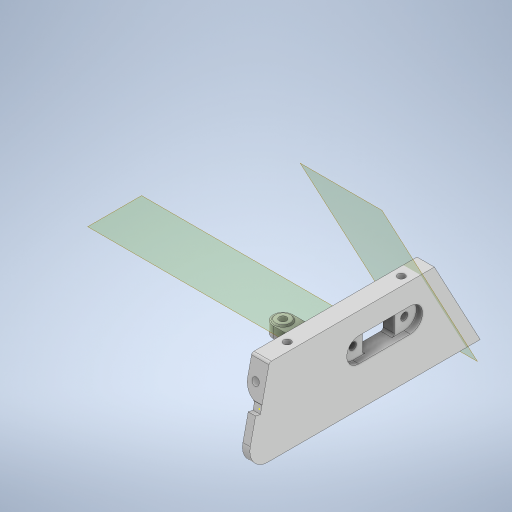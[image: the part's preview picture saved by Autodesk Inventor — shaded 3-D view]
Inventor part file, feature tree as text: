
AUTODESK INVENTOR PART (.ipt)
format: ipt  version: 2023 (Build 270158000, 158)  size: 805,888 bytes
history: native  units: mm
features: extrude x29, sketch x29, reference x17, other x16, projected_geometry x15, fillet x9, chamfer x1
ambient origin geometry x8: Origin, YZ Plane, XZ Plane, XY Plane, X Axis, Y Axis, Z Axis, Center Point
bodies: Body1 (feature_tree)
feature tree (116):
  other  "Bryła1"
  extrude  "Wyciągnięcie proste1"  Depth=6.5mm TaperAngle=0.0deg
  extrude  "Wyciągnięcie proste2"  Depth=3.7mm TaperAngle=0.0deg
  extrude  "Wyciągnięcie proste3"  Depth=1.5mm TaperAngle=0.0deg
  extrude  "Wyciągnięcie proste4"  Depth=6.0mm
  extrude  "Wyciągnięcie proste5"  Depth=3.0mm TaperAngle=0.0deg
  extrude  "Wyciągnięcie proste6"  Depth=5.0mm
  extrude  "Wyciągnięcie proste7"  Depth=3.0mm
  fillet  "Zaokrąglenie1"  Radius=15.0mm
  extrude  "Wyciągnięcie proste8"  Depth=6.0mm
  fillet  "Zaokrąglenie2"  Radius=15.0mm
  fillet  "Zaokrąglenie3"  Radius=35.5mm
  extrude  "Wyciągnięcie proste9"  TaperAngle=0.0deg  [1 undecoded]
  other  "Płaszczyzna konstrukcyjna1"
  extrude  "Wyciągnięcie proste12"  Depth=5.0mm
  extrude  "Wyciągnięcie proste13"  Depth=10.0mm TaperAngle=0.0deg
  other  "Płaszczyzna konstrukcyjna2"
  extrude  "Wyciągnięcie proste14"  Depth=3.5mm
  extrude  "Wyciągnięcie proste15"  Depth=2.0mm
  chamfer  "Faza1"  Distance=7.22mm
  fillet  "Zaokrąglenie7"  Radius=3.0mm
  fillet  "Zaokrąglenie8"  Radius=15.0mm
  fillet  "Zaokrąglenie9"  [1 undecoded]
  extrude  "Wyciągnięcie proste16"  Depth=10.0mm
  extrude  "Wyciągnięcie proste17"  Depth=10.0mm
  fillet  "Zaokrąglenie10"  Radius=7.0mm
  sketch  "Szkic18"
  other  "Płaszczyzna konstrukcyjna3"
  extrude  "Wyciągnięcie proste18"  Depth=7.0mm TaperAngle=0.0deg
  sketch  "Szkic19"
  extrude  "Wyciągnięcie proste19"  Depth=8.0mm
  extrude  "Wyciągnięcie proste20"  Depth=5.0mm TaperAngle=0.0deg
  fillet  "Zaokrąglenie11"  Radius=7.0mm
  extrude  "Wyciągnięcie proste21"  Depth=0.5mm TaperAngle=0.0deg
  extrude  "Wyciągnięcie proste22"  Depth=2.0mm TaperAngle=45.0deg
  extrude  "Wyciągnięcie proste23"  Depth=3.5mm
  sketch  "Szkic25"
  extrude  "Wyciągnięcie proste24"  Depth=2.0mm
  extrude  "Wyciągnięcie proste25"  Depth=4.0mm
  extrude  "Wyciągnięcie proste26"  Depth=10.0mm TaperAngle=0.0deg
  fillet  "Zaokrąglenie12"  Radius=13.0mm
  extrude  "Wyciągnięcie proste27"  Depth=10.0mm
  extrude  "Wyciągnięcie proste28"  TaperAngle=0.0deg  [1 undecoded]
  other  "Płaszczyzna konstrukcyjna4"
  extrude  "Wyciągnięcie proste29"  Depth=1.0mm
  extrude  "Wyciągnięcie proste30"  Depth=10.0mm TaperAngle=0.0deg
  extrude  "Wyciągnięcie proste31"  Depth=3.0mm TaperAngle=0.0deg
  sketch  "Szkic1"
  sketch  "Szkic2"
  sketch  "Szkic3"
  sketch  "Szkic4"
  sketch  "Szkic5"
  sketch  "Szkic6"
  projected_geometry  "Pętla rzutowana1"
  sketch  "Szkic7"
  sketch  "Szkic8"
  projected_geometry  "Pętla rzutowana2"
  sketch  "Szkic9"
  sketch  "Szkic12"
  reference  "Odniesienie1"
  reference  "Odniesienie2"
  sketch  "Szkic13"
  sketch  "Szkic14"
  reference  "Odniesienie3"
  sketch  "Szkic15"
  projected_geometry  "Pętla rzutowana3"
  sketch  "Szkic16"
  projected_geometry  "Pętla rzutowana4"
  sketch  "Szkic17"
  reference  "Odniesienie4"
  reference  "Odniesienie5"
  reference  "Odniesienie6"
  reference  "Odniesienie7"
  projected_geometry  "Pętla rzutowana5"
  sketch  "Szkic20"
  projected_geometry  "Pętla rzutowana6"
  reference  "Odniesienie8"
  sketch  "Szkic21"
  projected_geometry  "Pętla rzutowana7"
  sketch  "Szkic22"
  projected_geometry  "Pętla rzutowana8"
  reference  "Odniesienie9"
  reference  "Odniesienie10"
  sketch  "Szkic23"
  sketch  "Szkic24"
  projected_geometry  "Pętla rzutowana9"
  sketch  "Szkic26"
  projected_geometry  "Pętla rzutowana10"
  reference  "Odniesienie11"
  sketch  "Szkic27"
  reference  "Odniesienie12"
  reference  "Odniesienie13"
  reference  "Odniesienie14"
  reference  "Odniesienie15"
  sketch  "Szkic28"
  reference  "Odniesienie16"
  reference  "Odniesienie17"
  sketch  "Szkic29"
  projected_geometry  "Pętla rzutowana11"
  projected_geometry  "Pętla rzutowana12"
  projected_geometry  "Pętla rzutowana13"
  sketch  "Szkic30"
  sketch  "Szkic31"
  projected_geometry  "Pętla rzutowana14"
  projected_geometry  "Pętla rzutowana15"
  other  "<userpath>\Desktop\MojeRoboty\Stefan\mechanics 2\STEFAN.iam"
  other  "STEFAN.iam"
  other  "plytka_dol:1"
  other  "ARDUINO_NANO:1"
  other  "board_up:1"
  other  "koło_minisumo:2"
  other  "podstawa:1"
  other  "plug_2:1"
  other  "tylna:1"
  other  "mocowanie sharpow:1"
  other  "plug_kopia:1"
note: 3 required parameter values undecoded (feature->parameter linkage not recoverable at this tier; creation-order binding heuristic only, values carry confidence <= 0.55)
